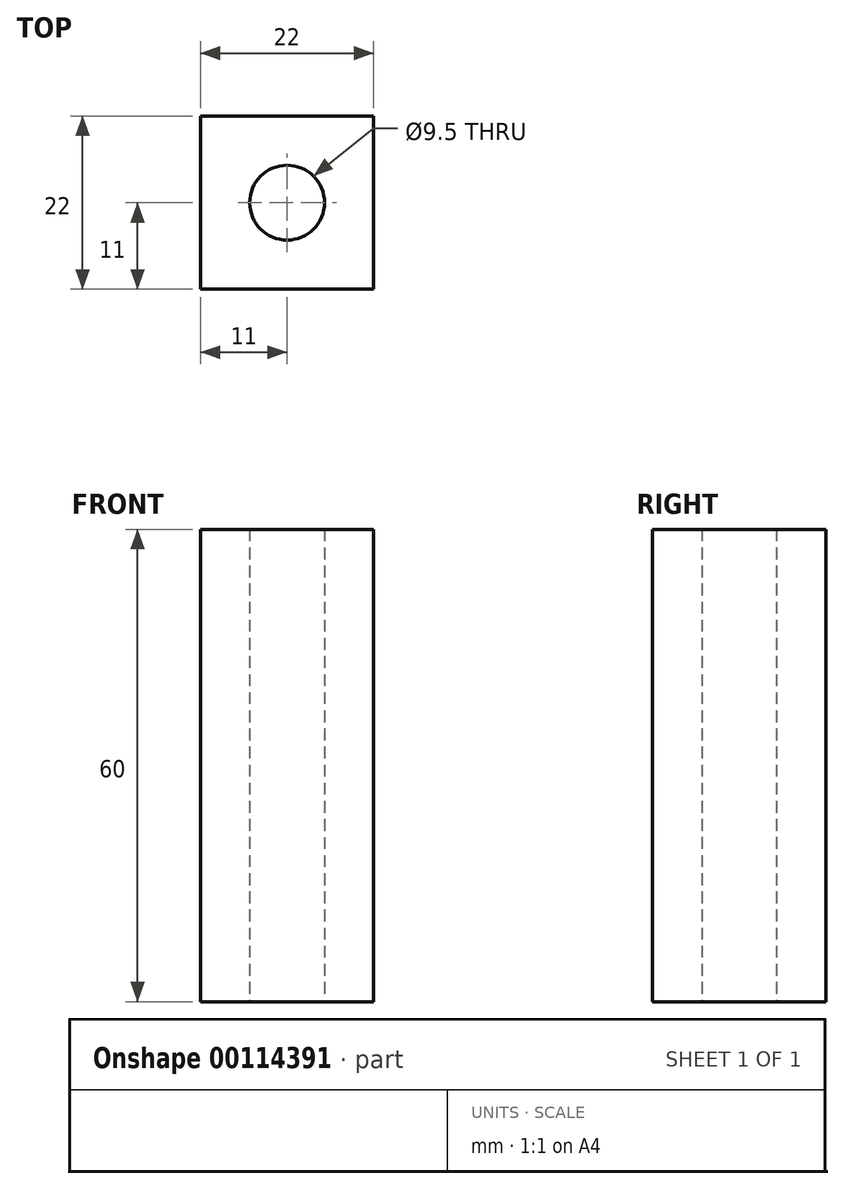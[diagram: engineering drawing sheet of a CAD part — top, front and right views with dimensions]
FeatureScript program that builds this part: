
annotation { "Feature Type Name" : "Feature", "Feature Type Description" : "" }
export const myFeature = defineFeature(function(context is Context, id is Id, definition is map)
    precondition{}
    {
        {
            var Q0;
            Q0=qCreatedBy(makeId("Top.planeOp"),FACE);
            var sketch = newSketch(context, id + "F0", { "sketchPlane" : qUnion([Q0])});
            skLineSegment(sketch, "E0.bottom", {"start": v(11, 11) * mm, "end": v(-11, 11) * mm});
            skLineSegment(sketch, "E0.top", {"start": v(11, -11) * mm, "end": v(-11, -11) * mm});
            skLineSegment(sketch, "E0.left", {"start": v(11, 11) * mm, "end": v(11, -11) * mm});
            skLineSegment(sketch, "E0.right", {"start": v(-11, 11) * mm, "end": v(-11, -11) * mm});
            skPoint(sketch, "E0.middle", {"position": v(0, 0) * mm});
            skCircle(sketch, "E1", {"center": v(0, 0) * mm, "radius": 4.75 * mm});
            skSolve(sketch);
        }
        {
            var Q0;
            Q0=makeQuery(id+"F0.imprint","IMPRINT",FACE,{"disambiguationData":[TD([[makeQuery(id+"F0.imprint","IMPRINT",EDGE,{"derivedFrom":sQuery(id+"F0.wireOp",EDGE,"E0.bottom")}),1.0]])]});
            extrude(context, id + "F1", {"entities" : qUnion([Q0]), "depth" : 60 * mm});
        }
    });
